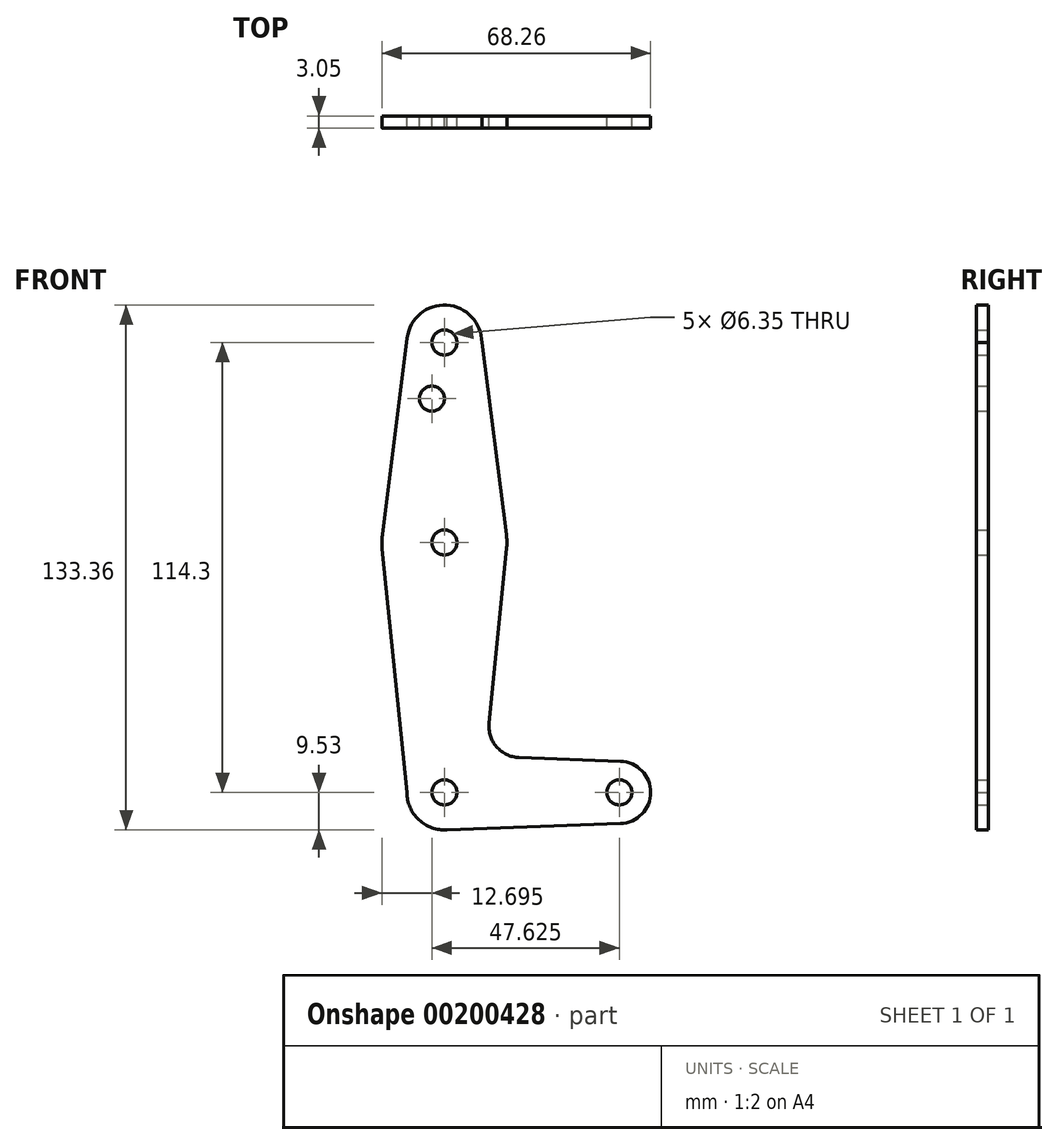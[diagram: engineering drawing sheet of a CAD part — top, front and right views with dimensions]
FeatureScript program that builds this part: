
annotation { "Feature Type Name" : "Feature", "Feature Type Description" : "" }
export const myFeature = defineFeature(function(context is Context, id is Id, definition is map)
    precondition{}
    {
        {
            var Q0;
            Q0=qCreatedBy(makeId("Front.planeOp"),FACE);
            var sketch = newSketch(context, id + "F0", { "sketchPlane" : qUnion([Q0])});
            skCircle(sketch, "E0", {"center": v(0, 0) * mm, "radius": 9.53 * mm});
            skLineSegment(sketch, "E1", {"start": v(0, 0) * mm, "end": v(0, 114.3) * mm, "construction": true});
            skCircle(sketch, "E2", {"center": v(0, 114.3) * mm, "radius": 9.52 * mm});
            skCircle(sketch, "E3", {"center": v(0, 63.5) * mm, "radius": 15.88 * mm});
            skLineSegment(sketch, "E4", {"start": v(0, 0) * mm, "end": v(44.45, 0) * mm, "construction": true});
            skCircle(sketch, "E5", {"center": v(44.45, 0) * mm, "radius": 7.94 * mm});
            skLineSegment(sketch, "E6", {"start": v(9.52, 114.3) * mm, "end": v(15.75, 65.5) * mm});
            skLineSegment(sketch, "E7", {"start": v(15.8, 61.91) * mm, "end": v(11.34, 17.6) * mm});
            skLineSegment(sketch, "E8", {"start": v(-9.53, 0) * mm, "end": v(-15.8, 61.9) * mm});
            skLineSegment(sketch, "E9", {"start": v(-15.75, 65.48) * mm, "end": v(-9.45, 115.5) * mm});
            skCircle(sketch, "E10", {"center": v(0, 114.3) * mm, "radius": 3.18 * mm});
            skCircle(sketch, "E11", {"center": v(0, 63.5) * mm, "radius": 3.18 * mm});
            skCircle(sketch, "E12", {"center": v(0, 0) * mm, "radius": 3.18 * mm});
            skCircle(sketch, "E13", {"center": v(-3.18, 100.03) * mm, "radius": 3.18 * mm});
            skCircle(sketch, "E14", {"center": v(44.45, 0) * mm, "radius": 3.18 * mm});
            skLineSegment(sketch, "E15", {"start": v(18.97, 8.85) * mm, "end": v(44.73, 7.93) * mm});
            skLineSegment(sketch, "E16", {"start": v(0, -9.53) * mm, "end": v(44.73, -7.93) * mm});
            skPoint(sketch, "E17.newPointA", {"position": v(9.57, 0) * mm});
            skPoint(sketch, "E17.newPointB", {"position": v(0, 9.53) * mm});
            skArc(sketch, "E17.filletArc", {"start": v(11.34, 17.6) * mm, "mid": v(13.26, 11.57) * mm, "end": v(18.97, 8.85) * mm});
            skSolve(sketch);
        }
        {
            var Q0;
            Q0 = qSketchRegion(id + "F0", true);
            extrude(context, id + "F1", {"entities" : qUnion([Q0]), "depth" : 3.05 * mm});
        }
    });
